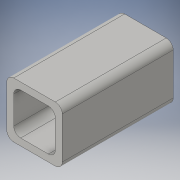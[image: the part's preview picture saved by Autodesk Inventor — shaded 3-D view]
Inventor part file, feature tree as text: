
AUTODESK INVENTOR PART (.ipt)
format: ipt  version: 2016 (Build 200138000, 138)  size: 113,664 bytes
history: native  units: in
note: dims shown in document units (in); Inventor stores cm internally (conversion verified against a paired STEP export)
features: extrude x1, sketch x1
ambient origin geometry x8: Origin, YZ Plane, XZ Plane, XY Plane, X Axis, Y Axis, Z Axis, Center Point
bodies: Solid1 (feature_tree)
feature tree (2):
  extrude  "Extrusion1"  Depth=1.0in
  sketch  "Sketch1"  dims[d0=1.0in d1=1.0in d2=0.125in d3=0.125in d4=2.0in d5=0.0in]
